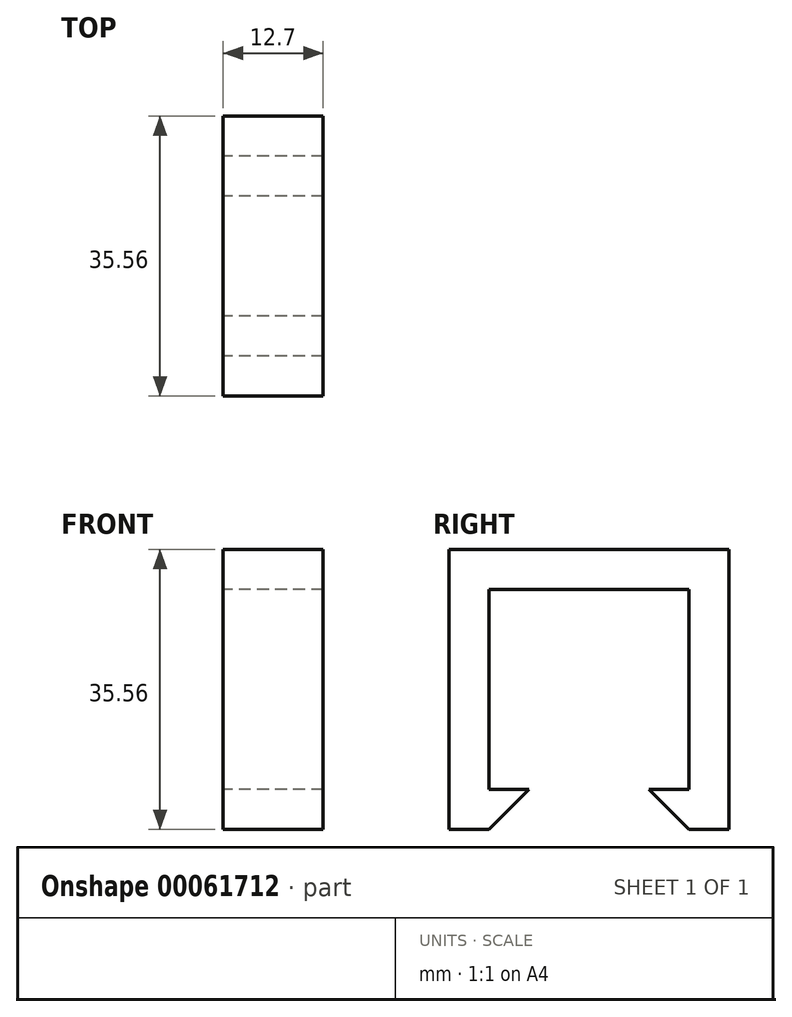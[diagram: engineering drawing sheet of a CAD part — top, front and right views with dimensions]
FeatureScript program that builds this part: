
annotation { "Feature Type Name" : "Feature", "Feature Type Description" : "" }
export const myFeature = defineFeature(function(context is Context, id is Id, definition is map)
    precondition{}
    {
        {
            var Q0;
            Q0=qCreatedBy(makeId("Right.planeOp"),FACE);
            var sketch = newSketch(context, id + "F0", { "sketchPlane" : qUnion([Q0])});
            skLineSegment(sketch, "E0", {"start": v(0, 0) * mm, "end": v(5.08, 0) * mm});
            skLineSegment(sketch, "E1", {"start": v(5.08, 0) * mm, "end": v(0, -5.08) * mm});
            skLineSegment(sketch, "E2", {"start": v(0, -5.08) * mm, "end": v(-5.08, -5.08) * mm});
            skLineSegment(sketch, "E3", {"start": v(-5.08, -5.08) * mm, "end": v(-5.08, 30.48) * mm});
            skLineSegment(sketch, "E4", {"start": v(-5.08, 30.48) * mm, "end": v(30.48, 30.48) * mm});
            skLineSegment(sketch, "E5", {"start": v(30.48, 30.48) * mm, "end": v(30.48, -5.08) * mm});
            skLineSegment(sketch, "E6", {"start": v(30.48, -5.08) * mm, "end": v(25.4, -5.08) * mm});
            skLineSegment(sketch, "E7", {"start": v(25.4, -5.08) * mm, "end": v(20.32, 0) * mm});
            skLineSegment(sketch, "E8", {"start": v(20.32, 0) * mm, "end": v(25.4, 0) * mm});
            skLineSegment(sketch, "E9", {"start": v(25.4, 0) * mm, "end": v(25.4, 25.4) * mm});
            skLineSegment(sketch, "E10", {"start": v(25.4, 25.4) * mm, "end": v(0, 25.4) * mm});
            skLineSegment(sketch, "E11", {"start": v(0, 25.4) * mm, "end": v(0, 0) * mm});
            skSolve(sketch);
        }
        {
            var Q0;
            Q0=makeQuery(id+"F0.imprint","IMPRINT",FACE,{"disambiguationData":[TD([[makeQuery(id+"F0.imprint","IMPRINT",EDGE,{"derivedFrom":sQuery(id+"F0.wireOp",EDGE,"E0")}),-1.0]])]});
            extrude(context, id + "F1", {"entities" : qUnion([Q0]), "endBound" : BoundingType.SYMMETRIC, "depth" : 12.7 * mm});
        }
    });
